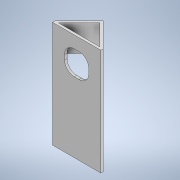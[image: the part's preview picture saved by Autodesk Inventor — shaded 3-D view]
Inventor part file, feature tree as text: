
AUTODESK INVENTOR PART (.ipt)
format: ipt  version: 2020 (Build 240168000, 168)  size: 137,728 bytes
history: native  units: mm
features: extrude x3, sketch x3
ambient origin geometry x8: Origin, YZ Plane, XZ Plane, XY Plane, X Axis, Y Axis, Z Axis, Center Point
bodies: Solid1 (feature_tree)
feature tree (6):
  extrude  "Extrusion1"  Depth=220.0mm
  extrude  "Extrusion2"  TaperAngle=45.0deg  [1 undecoded]
  extrude  "Extrusion5"  Depth=5.0mm
  sketch  "Sketch1"  dims[d0=100.0mm d1=220.0mm]
  sketch  "Sketch2"  dims[d2=5.0mm d3=0.0mm d4=45.0deg]
  sketch  "Sketch5"  dims[d5=5.0mm d6=5.0mm d7=55.0mm d8=0.0mm d16=50.0mm d17=50.0mm d18=20.0mm d19=5.0mm d20=0.0mm]
note: 1 required parameter value undecoded (feature->parameter linkage not recoverable at this tier; creation-order binding heuristic only, values carry confidence <= 0.55)
